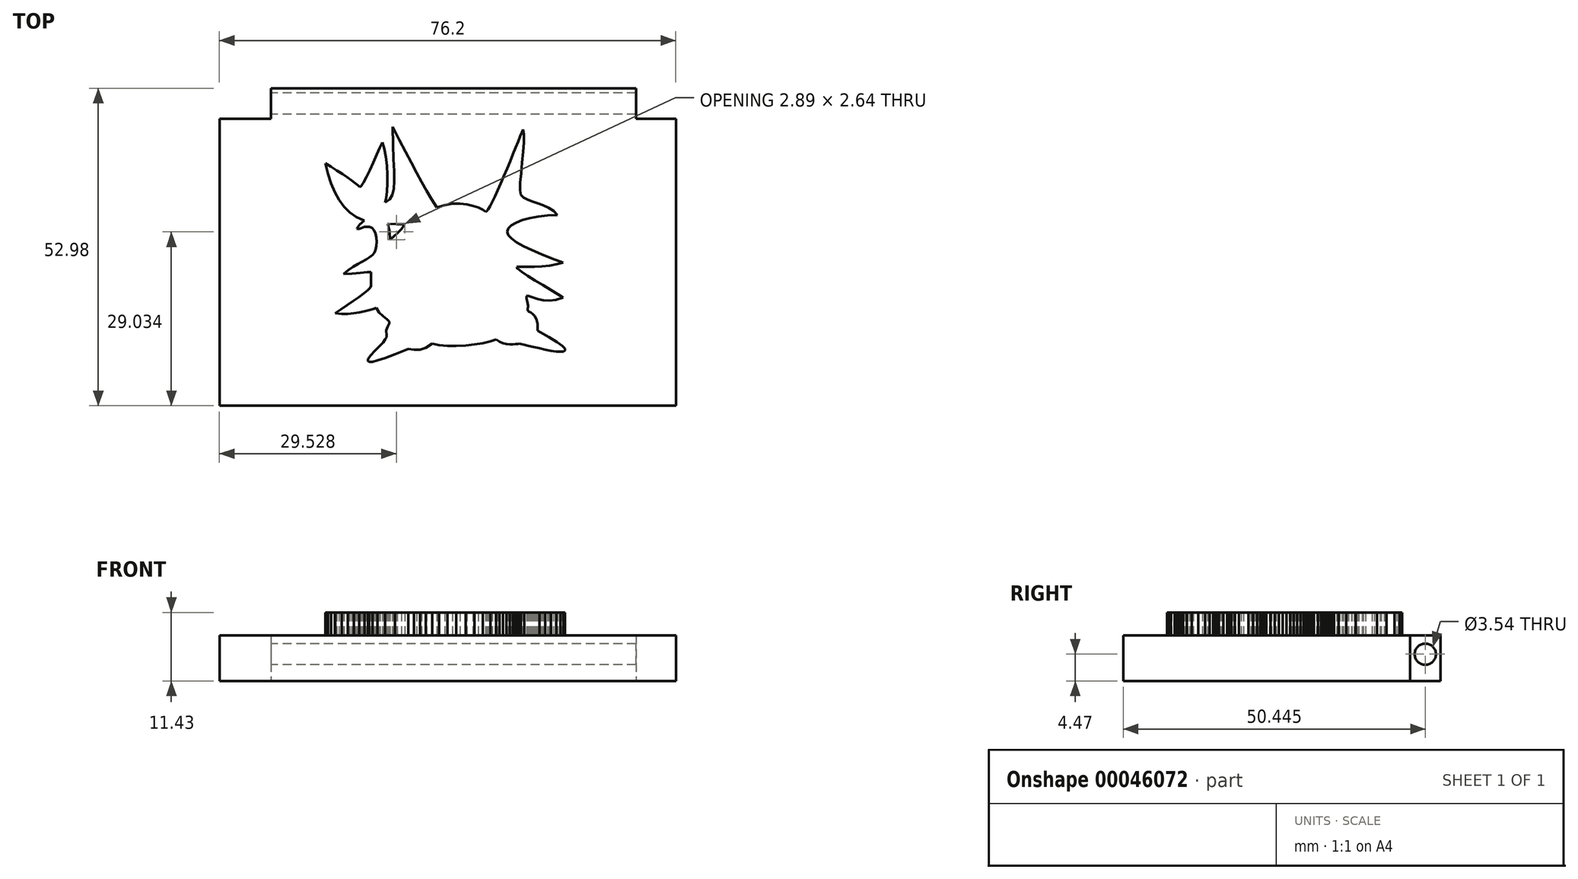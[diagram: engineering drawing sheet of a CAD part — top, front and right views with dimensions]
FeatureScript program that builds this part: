
annotation { "Feature Type Name" : "Feature", "Feature Type Description" : "" }
export const myFeature = defineFeature(function(context is Context, id is Id, definition is map)
    precondition{}
    {
        {
            var Q0;
            Q0=qCreatedBy(makeId("Top.planeOp"),FACE);
            var sketch = newSketch(context, id + "F0", { "sketchPlane" : qUnion([Q0])});
            skLineSegment(sketch, "E0.bottom", {"start": v(-26.13, 37.9) * mm, "end": v(34.83, 37.9) * mm});
            skLineSegment(sketch, "E0.top", {"start": v(-26.13, 32.81) * mm, "end": v(34.83, 32.81) * mm});
            skLineSegment(sketch, "E0.left", {"start": v(-26.13, 37.9) * mm, "end": v(-26.13, 32.81) * mm});
            skLineSegment(sketch, "E0.right", {"start": v(34.83, 37.9) * mm, "end": v(34.83, 32.81) * mm});
            skLineSegment(sketch, "E1.bottom", {"start": v(-34.73, 32.81) * mm, "end": v(41.47, 32.81) * mm});
            skLineSegment(sketch, "E1.top", {"start": v(-34.73, -15.09) * mm, "end": v(41.47, -15.09) * mm});
            skLineSegment(sketch, "E1.left", {"start": v(-34.73, 32.81) * mm, "end": v(-34.73, -15.09) * mm});
            skLineSegment(sketch, "E1.right", {"start": v(41.47, 32.81) * mm, "end": v(41.47, -15.09) * mm});
            skSolve(sketch);
        }
        {
            var Q0;
            Q0=makeQuery(id+"F0.imprint","IMPRINT",FACE,{"disambiguationData":[TD([[makeQuery(id+"F0.imprint","IMPRINT",EDGE,{"derivedFrom":sQuery(id+"F0.wireOp",EDGE,"E1.top")}),1.0]])]});
            var Q1;
            Q1=makeQuery(id+"F0.imprint","IMPRINT",FACE,{"disambiguationData":[TD([[makeQuery(id+"F0.imprint","IMPRINT",EDGE,{"derivedFrom":sQuery(id+"F0.wireOp",EDGE,"E0.bottom")}),-1.0]])]});
            extrude(context, id + "F1", {"entities" : qUnion([Q0, Q1]), "depth" : 7.62 * mm});
        }
        {
            var Q0;
            Q0=makeQuery(id+"F1.opExtrude","SWEPT_FACE",FACE,{"disambiguationData":[OSD([sQuery(id+"F0.wireOp",EDGE,"E0.left")])]});
            var sketch = newSketch(context, id + "F2", { "sketchPlane" : qUnion([Q0])});
            skLineSegment(sketch, "E2", {"start": v(-35.35, 7.62) * mm, "end": v(-35.35, 6.25) * mm});
            skLineSegment(sketch, "E3", {"start": v(-35.35, 6.25) * mm, "end": v(-37.9, 6.25) * mm});
            skLineSegment(sketch, "E4", {"start": v(-35.35, 6.25) * mm, "end": v(-35.35, 4.47) * mm});
            skCircle(sketch, "E5", {"center": v(-35.35, 4.47) * mm, "radius": 1.77 * mm});
            skLineSegment(sketch, "E6", {"start": v(-35.35, 4.47) * mm, "end": v(-37.12, 4.47) * mm});
            skSolve(sketch);
        }
        {
            var Q0;
            {var subQ0=sQuery(id+"F2.wireOp",EDGE,"E6");Q0=makeQuery(id+"F2.imprint","IMPRINT",FACE,{"disambiguationData":[TD([[makeQuery(id+"F2.imprint","IMPRINT",EDGE,{"derivedFrom":subQ0}),-1.0]])]});}
            var Q1;
            {var subQ0=sQuery(id+"F2.wireOp",EDGE,"E6");Q1=makeQuery(id+"F2.imprint","IMPRINT",FACE,{"disambiguationData":[TD([[makeQuery(id+"F2.imprint","IMPRINT",EDGE,{"derivedFrom":subQ0}),1.0]])]});}
            extrude(context, id + "F3", {"entities" : qUnion([Q0, Q1]), "operationType" : NewBodyOperationType.REMOVE, "oppositeDirection" : true, "depth" : 127 * mm});
        }
        {
            var Q0;
            Q0=makeQuery(id+"F1.opExtrude","CAP_FACE",FACE,{"disambiguationData":[OSD([sQuery(id+"F0.wireOp",EDGE,"E0.bottom"),sQuery(id+"F0.wireOp",EDGE,"E0.left"),sQuery(id+"F0.wireOp",EDGE,"E0.right"),sQuery(id+"F0.wireOp",EDGE,"E1.bottom"),sQuery(id+"F0.wireOp",EDGE,"E1.top"),sQuery(id+"F0.wireOp",EDGE,"E1.left"),sQuery(id+"F0.wireOp",EDGE,"E1.right")])],"isStart":false});
            var sketch = newSketch(context, id + "F4", { "sketchPlane" : qUnion([Q0])});
            skLineSegment(sketch, "E7", {"start": v(-8.8, 19.62) * mm, "end": v(-7.67, 17.43) * mm});
            skLineSegment(sketch, "E8", {"start": v(-7.67, 17.43) * mm, "end": v(-6.63, 15.44) * mm});
            skLineSegment(sketch, "E9", {"start": v(-6.63, 15.44) * mm, "end": v(-5.68, 13.62) * mm});
            skLineSegment(sketch, "E10", {"start": v(-5.68, 13.62) * mm, "end": v(-4.78, 11.94) * mm});
            skLineSegment(sketch, "E11", {"start": v(-4.78, 11.94) * mm, "end": v(-3.93, 10.39) * mm});
            skLineSegment(sketch, "E12", {"start": v(-3.93, 10.39) * mm, "end": v(-3.1, 8.93) * mm});
            skLineSegment(sketch, "E13", {"start": v(-3.1, 8.93) * mm, "end": v(-2.27, 7.52) * mm});
            skLineSegment(sketch, "E14", {"start": v(-2.27, 7.52) * mm, "end": v(-1.42, 6.16) * mm});
            skLineSegment(sketch, "E15", {"start": v(-1.42, 6.16) * mm, "end": v(-0.09, 6.56) * mm});
            skLineSegment(sketch, "E16", {"start": v(-0.09, 6.56) * mm, "end": v(1.21, 6.76) * mm});
            skLineSegment(sketch, "E17", {"start": v(1.21, 6.76) * mm, "end": v(2.46, 6.78) * mm});
            skLineSegment(sketch, "E18", {"start": v(2.46, 6.78) * mm, "end": v(3.62, 6.66) * mm});
            skLineSegment(sketch, "E19", {"start": v(3.62, 6.66) * mm, "end": v(4.66, 6.43) * mm});
            skLineSegment(sketch, "E20", {"start": v(4.66, 6.43) * mm, "end": v(5.55, 6.13) * mm});
            skLineSegment(sketch, "E21", {"start": v(5.55, 6.13) * mm, "end": v(6.25, 5.8) * mm});
            skLineSegment(sketch, "E22", {"start": v(6.25, 5.8) * mm, "end": v(6.75, 5.46) * mm});
            skLineSegment(sketch, "E23", {"start": v(6.75, 5.46) * mm, "end": v(6.91, 5.5) * mm});
            skLineSegment(sketch, "E24", {"start": v(6.91, 5.5) * mm, "end": v(7.17, 5.81) * mm});
            skLineSegment(sketch, "E25", {"start": v(7.17, 5.81) * mm, "end": v(7.49, 6.35) * mm});
            skLineSegment(sketch, "E26", {"start": v(7.49, 6.35) * mm, "end": v(7.87, 7.1) * mm});
            skLineSegment(sketch, "E27", {"start": v(7.87, 7.1) * mm, "end": v(8.3, 8) * mm});
            skLineSegment(sketch, "E28", {"start": v(8.3, 8) * mm, "end": v(8.78, 9.04) * mm});
            skLineSegment(sketch, "E29", {"start": v(8.78, 9.04) * mm, "end": v(9.28, 10.17) * mm});
            skLineSegment(sketch, "E30", {"start": v(9.28, 10.17) * mm, "end": v(9.8, 11.37) * mm});
            skLineSegment(sketch, "E31", {"start": v(9.8, 11.37) * mm, "end": v(10.3, 12.6) * mm});
            skLineSegment(sketch, "E32", {"start": v(10.3, 12.6) * mm, "end": v(10.82, 13.83) * mm});
            skLineSegment(sketch, "E33", {"start": v(10.82, 13.83) * mm, "end": v(11.3, 15.01) * mm});
            skLineSegment(sketch, "E34", {"start": v(11.3, 15.01) * mm, "end": v(11.75, 16.13) * mm});
            skLineSegment(sketch, "E35", {"start": v(11.75, 16.13) * mm, "end": v(12.16, 17.14) * mm});
            skLineSegment(sketch, "E36", {"start": v(12.16, 17.14) * mm, "end": v(12.51, 18) * mm});
            skLineSegment(sketch, "E37", {"start": v(12.51, 18) * mm, "end": v(12.8, 18.7) * mm});
            skLineSegment(sketch, "E38", {"start": v(12.8, 18.7) * mm, "end": v(13, 19.2) * mm});
            skLineSegment(sketch, "E39", {"start": v(13, 19.2) * mm, "end": v(13.16, 18.35) * mm});
            skLineSegment(sketch, "E40", {"start": v(13.16, 18.35) * mm, "end": v(13.15, 17.03) * mm});
            skLineSegment(sketch, "E41", {"start": v(13.15, 17.03) * mm, "end": v(13.02, 15.41) * mm});
            skLineSegment(sketch, "E42", {"start": v(13.02, 15.41) * mm, "end": v(12.84, 13.64) * mm});
            skLineSegment(sketch, "E43", {"start": v(12.84, 13.64) * mm, "end": v(12.66, 11.88) * mm});
            skLineSegment(sketch, "E44", {"start": v(12.66, 11.88) * mm, "end": v(12.53, 10.3) * mm});
            skLineSegment(sketch, "E45", {"start": v(12.53, 10.3) * mm, "end": v(12.51, 9.02) * mm});
            skLineSegment(sketch, "E46", {"start": v(12.51, 9.02) * mm, "end": v(12.66, 8.24) * mm});
            skLineSegment(sketch, "E47", {"start": v(12.66, 8.24) * mm, "end": v(13.04, 7.81) * mm});
            skLineSegment(sketch, "E48", {"start": v(13.04, 7.81) * mm, "end": v(13.68, 7.46) * mm});
            skLineSegment(sketch, "E49", {"start": v(13.68, 7.46) * mm, "end": v(14.48, 7.15) * mm});
            skLineSegment(sketch, "E50", {"start": v(14.48, 7.15) * mm, "end": v(15.39, 6.85) * mm});
            skLineSegment(sketch, "E51", {"start": v(15.39, 6.85) * mm, "end": v(16.33, 6.5) * mm});
            skLineSegment(sketch, "E52", {"start": v(16.33, 6.5) * mm, "end": v(17.25, 6.1) * mm});
            skLineSegment(sketch, "E53", {"start": v(17.25, 6.1) * mm, "end": v(18.06, 5.56) * mm});
            skLineSegment(sketch, "E54", {"start": v(18.06, 5.56) * mm, "end": v(18.7, 4.88) * mm});
            skLineSegment(sketch, "E55", {"start": v(18.7, 4.88) * mm, "end": v(17.1, 4.8) * mm});
            skLineSegment(sketch, "E56", {"start": v(17.1, 4.8) * mm, "end": v(15.56, 4.63) * mm});
            skLineSegment(sketch, "E57", {"start": v(15.56, 4.63) * mm, "end": v(14.15, 4.37) * mm});
            skLineSegment(sketch, "E58", {"start": v(14.15, 4.37) * mm, "end": v(12.89, 4.03) * mm});
            skLineSegment(sketch, "E59", {"start": v(12.89, 4.03) * mm, "end": v(11.83, 3.62) * mm});
            skLineSegment(sketch, "E60", {"start": v(11.83, 3.62) * mm, "end": v(11.03, 3.16) * mm});
            skLineSegment(sketch, "E61", {"start": v(11.03, 3.16) * mm, "end": v(10.51, 2.65) * mm});
            skLineSegment(sketch, "E62", {"start": v(10.51, 2.65) * mm, "end": v(10.33, 2.1) * mm});
            skLineSegment(sketch, "E63", {"start": v(10.33, 2.1) * mm, "end": v(10.53, 1.54) * mm});
            skLineSegment(sketch, "E64", {"start": v(10.53, 1.54) * mm, "end": v(11.08, 0.95) * mm});
            skLineSegment(sketch, "E65", {"start": v(11.08, 0.95) * mm, "end": v(11.94, 0.33) * mm});
            skLineSegment(sketch, "E66", {"start": v(11.94, 0.33) * mm, "end": v(13.09, -0.3) * mm});
            skLineSegment(sketch, "E67", {"start": v(13.09, -0.3) * mm, "end": v(14.47, -0.96) * mm});
            skLineSegment(sketch, "E68", {"start": v(14.47, -0.96) * mm, "end": v(16.06, -1.64) * mm});
            skLineSegment(sketch, "E69", {"start": v(16.06, -1.64) * mm, "end": v(17.8, -2.33) * mm});
            skLineSegment(sketch, "E70", {"start": v(17.8, -2.33) * mm, "end": v(19.67, -3.04) * mm});
            skLineSegment(sketch, "E71", {"start": v(19.67, -3.04) * mm, "end": v(18.63, -3.33) * mm});
            skLineSegment(sketch, "E72", {"start": v(18.63, -3.33) * mm, "end": v(17.42, -3.53) * mm});
            skLineSegment(sketch, "E73", {"start": v(17.42, -3.53) * mm, "end": v(16.14, -3.66) * mm});
            skLineSegment(sketch, "E74", {"start": v(16.14, -3.66) * mm, "end": v(14.89, -3.73) * mm});
            skLineSegment(sketch, "E75", {"start": v(14.89, -3.73) * mm, "end": v(13.75, -3.76) * mm});
            skLineSegment(sketch, "E76", {"start": v(13.75, -3.76) * mm, "end": v(12.82, -3.76) * mm});
            skLineSegment(sketch, "E77", {"start": v(12.82, -3.76) * mm, "end": v(12.19, -3.75) * mm});
            skLineSegment(sketch, "E78", {"start": v(12.19, -3.75) * mm, "end": v(11.96, -3.75) * mm});
            skLineSegment(sketch, "E79", {"start": v(11.96, -3.75) * mm, "end": v(12.1, -4.06) * mm});
            skLineSegment(sketch, "E80", {"start": v(12.1, -4.06) * mm, "end": v(12.75, -4.58) * mm});
            skLineSegment(sketch, "E81", {"start": v(12.75, -4.58) * mm, "end": v(13.75, -5.25) * mm});
            skLineSegment(sketch, "E82", {"start": v(13.75, -5.25) * mm, "end": v(15, -6.01) * mm});
            skLineSegment(sketch, "E83", {"start": v(15, -6.01) * mm, "end": v(16.34, -6.82) * mm});
            skLineSegment(sketch, "E84", {"start": v(16.34, -6.82) * mm, "end": v(17.65, -7.61) * mm});
            skLineSegment(sketch, "E85", {"start": v(17.65, -7.61) * mm, "end": v(18.8, -8.33) * mm});
            skLineSegment(sketch, "E86", {"start": v(18.8, -8.33) * mm, "end": v(19.68, -8.92) * mm});
            skLineSegment(sketch, "E87", {"start": v(19.68, -8.92) * mm, "end": v(18.49, -9.3) * mm});
            skLineSegment(sketch, "E88", {"start": v(18.49, -9.3) * mm, "end": v(17.37, -9.42) * mm});
            skLineSegment(sketch, "E89", {"start": v(17.37, -9.42) * mm, "end": v(16.35, -9.34) * mm});
            skLineSegment(sketch, "E90", {"start": v(16.35, -9.34) * mm, "end": v(15.46, -9.14) * mm});
            skLineSegment(sketch, "E91", {"start": v(15.46, -9.14) * mm, "end": v(14.71, -8.9) * mm});
            skLineSegment(sketch, "E92", {"start": v(14.71, -8.9) * mm, "end": v(14.14, -8.69) * mm});
            skLineSegment(sketch, "E93", {"start": v(14.14, -8.69) * mm, "end": v(13.76, -8.58) * mm});
            skLineSegment(sketch, "E94", {"start": v(13.76, -8.58) * mm, "end": v(13.6, -8.66) * mm});
            skLineSegment(sketch, "E95", {"start": v(13.6, -8.66) * mm, "end": v(13.6, -9.1) * mm});
            skLineSegment(sketch, "E96", {"start": v(13.6, -9.1) * mm, "end": v(13.7, -9.6) * mm});
            skLineSegment(sketch, "E97", {"start": v(13.7, -9.6) * mm, "end": v(13.8, -10.22) * mm});
            skLineSegment(sketch, "E98", {"start": v(13.8, -10.22) * mm, "end": v(13.78, -10.96) * mm});
            skLineSegment(sketch, "E99", {"start": v(13.78, -10.96) * mm, "end": v(13.8, -11.13) * mm});
            skLineSegment(sketch, "E100", {"start": v(13.8, -11.13) * mm, "end": v(13.99, -11.26) * mm});
            skLineSegment(sketch, "E101", {"start": v(13.99, -11.26) * mm, "end": v(14.27, -11.4) * mm});
            skLineSegment(sketch, "E102", {"start": v(14.27, -11.4) * mm, "end": v(14.6, -11.6) * mm});
            skLineSegment(sketch, "E103", {"start": v(14.6, -11.6) * mm, "end": v(14.94, -11.95) * mm});
            skLineSegment(sketch, "E104", {"start": v(14.94, -11.95) * mm, "end": v(15.23, -12.5) * mm});
            skLineSegment(sketch, "E105", {"start": v(15.23, -12.5) * mm, "end": v(15.4, -13.3) * mm});
            skLineSegment(sketch, "E106", {"start": v(15.4, -13.3) * mm, "end": v(15.44, -14.43) * mm});
            skLineSegment(sketch, "E107", {"start": v(15.44, -14.43) * mm, "end": v(17.33, -15.5) * mm});
            skLineSegment(sketch, "E108", {"start": v(17.33, -15.5) * mm, "end": v(18.68, -16.34) * mm});
            skLineSegment(sketch, "E109", {"start": v(18.68, -16.34) * mm, "end": v(19.54, -16.98) * mm});
            skLineSegment(sketch, "E110", {"start": v(19.54, -16.98) * mm, "end": v(19.97, -17.43) * mm});
            skLineSegment(sketch, "E111", {"start": v(19.97, -17.43) * mm, "end": v(20.02, -17.73) * mm});
            skLineSegment(sketch, "E112", {"start": v(20.02, -17.73) * mm, "end": v(19.76, -17.9) * mm});
            skLineSegment(sketch, "E113", {"start": v(19.76, -17.9) * mm, "end": v(19.24, -17.94) * mm});
            skLineSegment(sketch, "E114", {"start": v(19.24, -17.94) * mm, "end": v(18.52, -17.88) * mm});
            skLineSegment(sketch, "E115", {"start": v(18.52, -17.88) * mm, "end": v(17.65, -17.76) * mm});
            skLineSegment(sketch, "E116", {"start": v(17.65, -17.76) * mm, "end": v(16.7, -17.58) * mm});
            skLineSegment(sketch, "E117", {"start": v(16.7, -17.58) * mm, "end": v(15.72, -17.37) * mm});
            skLineSegment(sketch, "E118", {"start": v(15.72, -17.37) * mm, "end": v(14.77, -17.15) * mm});
            skLineSegment(sketch, "E119", {"start": v(14.77, -17.15) * mm, "end": v(13.9, -16.94) * mm});
            skLineSegment(sketch, "E120", {"start": v(13.9, -16.94) * mm, "end": v(13.18, -16.77) * mm});
            skLineSegment(sketch, "E121", {"start": v(13.18, -16.77) * mm, "end": v(12.66, -16.65) * mm});
            skLineSegment(sketch, "E122", {"start": v(12.66, -16.65) * mm, "end": v(12.4, -16.6) * mm});
            skLineSegment(sketch, "E123", {"start": v(12.4, -16.6) * mm, "end": v(12.11, -16.63) * mm});
            skLineSegment(sketch, "E124", {"start": v(12.11, -16.63) * mm, "end": v(11.73, -16.67) * mm});
            skLineSegment(sketch, "E125", {"start": v(11.73, -16.67) * mm, "end": v(11.28, -16.7) * mm});
            skLineSegment(sketch, "E126", {"start": v(11.28, -16.7) * mm, "end": v(10.77, -16.7) * mm});
            skLineSegment(sketch, "E127", {"start": v(10.77, -16.7) * mm, "end": v(10.21, -16.66) * mm});
            skLineSegment(sketch, "E128", {"start": v(10.21, -16.66) * mm, "end": v(9.63, -16.53) * mm});
            skLineSegment(sketch, "E129", {"start": v(9.63, -16.53) * mm, "end": v(9.05, -16.28) * mm});
            skLineSegment(sketch, "E130", {"start": v(9.05, -16.28) * mm, "end": v(8.48, -15.91) * mm});
            skLineSegment(sketch, "E131", {"start": v(8.48, -15.91) * mm, "end": v(7.52, -16.21) * mm});
            skLineSegment(sketch, "E132", {"start": v(7.52, -16.21) * mm, "end": v(6.3, -16.49) * mm});
            skLineSegment(sketch, "E133", {"start": v(6.3, -16.49) * mm, "end": v(4.9, -16.72) * mm});
            skLineSegment(sketch, "E134", {"start": v(4.9, -16.72) * mm, "end": v(3.39, -16.89) * mm});
            skLineSegment(sketch, "E135", {"start": v(3.39, -16.89) * mm, "end": v(1.85, -16.97) * mm});
            skLineSegment(sketch, "E136", {"start": v(1.85, -16.97) * mm, "end": v(0.35, -16.97) * mm});
            skLineSegment(sketch, "E137", {"start": v(0.35, -16.97) * mm, "end": v(-1.02, -16.85) * mm});
            skLineSegment(sketch, "E138", {"start": v(-1.02, -16.85) * mm, "end": v(-2.2, -16.6) * mm});
            skLineSegment(sketch, "E139", {"start": v(-2.2, -16.6) * mm, "end": v(-3.22, -17.28) * mm});
            skLineSegment(sketch, "E140", {"start": v(-3.22, -17.28) * mm, "end": v(-4.21, -17.58) * mm});
            skLineSegment(sketch, "E141", {"start": v(-4.21, -17.58) * mm, "end": v(-5.2, -17.61) * mm});
            skLineSegment(sketch, "E142", {"start": v(-5.2, -17.61) * mm, "end": v(-6.2, -17.48) * mm});
            skLineSegment(sketch, "E143", {"start": v(-6.2, -17.48) * mm, "end": v(-8.37, -18.36) * mm});
            skLineSegment(sketch, "E144", {"start": v(-8.37, -18.36) * mm, "end": v(-10.06, -19) * mm});
            skLineSegment(sketch, "E145", {"start": v(-10.06, -19) * mm, "end": v(-11.3, -19.4) * mm});
            skLineSegment(sketch, "E146", {"start": v(-11.3, -19.4) * mm, "end": v(-12.16, -19.6) * mm});
            skLineSegment(sketch, "E147", {"start": v(-12.16, -19.6) * mm, "end": v(-12.68, -19.62) * mm});
            skLineSegment(sketch, "E148", {"start": v(-12.68, -19.62) * mm, "end": v(-12.91, -19.5) * mm});
            skLineSegment(sketch, "E149", {"start": v(-12.91, -19.5) * mm, "end": v(-12.9, -19.24) * mm});
            skLineSegment(sketch, "E150", {"start": v(-12.9, -19.24) * mm, "end": v(-12.68, -18.87) * mm});
            skLineSegment(sketch, "E151", {"start": v(-12.68, -18.87) * mm, "end": v(-12.32, -18.43) * mm});
            skLineSegment(sketch, "E152", {"start": v(-12.32, -18.43) * mm, "end": v(-11.87, -17.94) * mm});
            skLineSegment(sketch, "E153", {"start": v(-11.87, -17.94) * mm, "end": v(-11.36, -17.41) * mm});
            skLineSegment(sketch, "E154", {"start": v(-11.36, -17.41) * mm, "end": v(-10.85, -16.88) * mm});
            skLineSegment(sketch, "E155", {"start": v(-10.85, -16.88) * mm, "end": v(-10.39, -16.37) * mm});
            skLineSegment(sketch, "E156", {"start": v(-10.39, -16.37) * mm, "end": v(-10.02, -15.9) * mm});
            skLineSegment(sketch, "E157", {"start": v(-10.02, -15.9) * mm, "end": v(-9.8, -15.52) * mm});
            skLineSegment(sketch, "E158", {"start": v(-9.8, -15.52) * mm, "end": v(-9.76, -15.22) * mm});
            skLineSegment(sketch, "E159", {"start": v(-9.76, -15.22) * mm, "end": v(-9.84, -14.36) * mm});
            skLineSegment(sketch, "E160", {"start": v(-9.84, -14.36) * mm, "end": v(-9.62, -13.72) * mm});
            skLineSegment(sketch, "E161", {"start": v(-9.62, -13.72) * mm, "end": v(-9.36, -13.24) * mm});
            skLineSegment(sketch, "E162", {"start": v(-9.36, -13.24) * mm, "end": v(-9.33, -12.87) * mm});
            skLineSegment(sketch, "E163", {"start": v(-9.33, -12.87) * mm, "end": v(-9.71, -12.49) * mm});
            skLineSegment(sketch, "E164", {"start": v(-9.71, -12.49) * mm, "end": v(-10.38, -12) * mm});
            skLineSegment(sketch, "E165", {"start": v(-10.38, -12) * mm, "end": v(-11.06, -11.38) * mm});
            skLineSegment(sketch, "E166", {"start": v(-11.06, -11.38) * mm, "end": v(-11.5, -10.61) * mm});
            skLineSegment(sketch, "E167", {"start": v(-11.5, -10.61) * mm, "end": v(-12.03, -10.79) * mm});
            skLineSegment(sketch, "E168", {"start": v(-12.03, -10.79) * mm, "end": v(-12.7, -10.99) * mm});
            skLineSegment(sketch, "E169", {"start": v(-12.7, -10.99) * mm, "end": v(-13.47, -11.19) * mm});
            skLineSegment(sketch, "E170", {"start": v(-13.47, -11.19) * mm, "end": v(-14.34, -11.37) * mm});
            skLineSegment(sketch, "E171", {"start": v(-14.34, -11.37) * mm, "end": v(-15.28, -11.52) * mm});
            skLineSegment(sketch, "E172", {"start": v(-15.28, -11.52) * mm, "end": v(-16.27, -11.6) * mm});
            skLineSegment(sketch, "E173", {"start": v(-16.27, -11.6) * mm, "end": v(-17.3, -11.6) * mm});
            skLineSegment(sketch, "E174", {"start": v(-17.3, -11.6) * mm, "end": v(-18.36, -11.5) * mm});
            skLineSegment(sketch, "E175", {"start": v(-18.36, -11.5) * mm, "end": v(-17.4, -10.85) * mm});
            skLineSegment(sketch, "E176", {"start": v(-17.4, -10.85) * mm, "end": v(-16.38, -10.18) * mm});
            skLineSegment(sketch, "E177", {"start": v(-16.38, -10.18) * mm, "end": v(-15.37, -9.5) * mm});
            skLineSegment(sketch, "E178", {"start": v(-15.37, -9.5) * mm, "end": v(-14.43, -8.84) * mm});
            skLineSegment(sketch, "E179", {"start": v(-14.43, -8.84) * mm, "end": v(-13.6, -8.23) * mm});
            skLineSegment(sketch, "E180", {"start": v(-13.6, -8.23) * mm, "end": v(-12.95, -7.68) * mm});
            skLineSegment(sketch, "E181", {"start": v(-12.95, -7.68) * mm, "end": v(-12.52, -7.23) * mm});
            skLineSegment(sketch, "E182", {"start": v(-12.52, -7.23) * mm, "end": v(-12.37, -6.9) * mm});
            skLineSegment(sketch, "E183", {"start": v(-12.37, -6.9) * mm, "end": v(-12.38, -6.3) * mm});
            skLineSegment(sketch, "E184", {"start": v(-12.38, -6.3) * mm, "end": v(-12.39, -5.66) * mm});
            skLineSegment(sketch, "E185", {"start": v(-12.39, -5.66) * mm, "end": v(-12.39, -5.06) * mm});
            skLineSegment(sketch, "E186", {"start": v(-12.39, -5.06) * mm, "end": v(-12.37, -4.62) * mm});
            skLineSegment(sketch, "E187", {"start": v(-12.37, -4.62) * mm, "end": v(-13.04, -4.66) * mm});
            skLineSegment(sketch, "E188", {"start": v(-13.04, -4.66) * mm, "end": v(-14.18, -4.77) * mm});
            skLineSegment(sketch, "E189", {"start": v(-14.18, -4.77) * mm, "end": v(-15.57, -4.89) * mm});
            skLineSegment(sketch, "E190", {"start": v(-15.57, -4.89) * mm, "end": v(-16.97, -4.96) * mm});
            skLineSegment(sketch, "E191", {"start": v(-16.97, -4.96) * mm, "end": v(-16.2, -4.32) * mm});
            skLineSegment(sketch, "E192", {"start": v(-16.2, -4.32) * mm, "end": v(-15.4, -3.78) * mm});
            skLineSegment(sketch, "E193", {"start": v(-15.4, -3.78) * mm, "end": v(-14.62, -3.31) * mm});
            skLineSegment(sketch, "E194", {"start": v(-14.62, -3.31) * mm, "end": v(-13.89, -2.9) * mm});
            skLineSegment(sketch, "E195", {"start": v(-13.89, -2.9) * mm, "end": v(-13.22, -2.52) * mm});
            skLineSegment(sketch, "E196", {"start": v(-13.22, -2.52) * mm, "end": v(-12.63, -2.16) * mm});
            skLineSegment(sketch, "E197", {"start": v(-12.63, -2.16) * mm, "end": v(-12.17, -1.8) * mm});
            skLineSegment(sketch, "E198", {"start": v(-12.17, -1.8) * mm, "end": v(-11.85, -1.4) * mm});
            skLineSegment(sketch, "E199", {"start": v(-11.85, -1.4) * mm, "end": v(-11.64, -0.9) * mm});
            skLineSegment(sketch, "E200", {"start": v(-11.64, -0.9) * mm, "end": v(-11.5, -0.29) * mm});
            skLineSegment(sketch, "E201", {"start": v(-11.5, -0.29) * mm, "end": v(-11.46, 0.4) * mm});
            skLineSegment(sketch, "E202", {"start": v(-11.46, 0.4) * mm, "end": v(-11.5, 1.12) * mm});
            skLineSegment(sketch, "E203", {"start": v(-11.5, 1.12) * mm, "end": v(-11.63, 1.78) * mm});
            skLineSegment(sketch, "E204", {"start": v(-11.63, 1.78) * mm, "end": v(-11.86, 2.35) * mm});
            skLineSegment(sketch, "E205", {"start": v(-11.86, 2.35) * mm, "end": v(-12.2, 2.75) * mm});
            skLineSegment(sketch, "E206", {"start": v(-12.2, 2.75) * mm, "end": v(-12.63, 2.94) * mm});
            skLineSegment(sketch, "E207", {"start": v(-12.63, 2.94) * mm, "end": v(-13.48, 2.9) * mm});
            skLineSegment(sketch, "E208", {"start": v(-13.48, 2.9) * mm, "end": v(-14.09, 2.69) * mm});
            skLineSegment(sketch, "E209", {"start": v(-14.09, 2.69) * mm, "end": v(-14.5, 2.52) * mm});
            skLineSegment(sketch, "E210", {"start": v(-14.5, 2.52) * mm, "end": v(-14.76, 2.63) * mm});
            skLineSegment(sketch, "E211", {"start": v(-14.76, 2.63) * mm, "end": v(-14.64, 2.87) * mm});
            skLineSegment(sketch, "E212", {"start": v(-14.64, 2.87) * mm, "end": v(-14.46, 3.11) * mm});
            skLineSegment(sketch, "E213", {"start": v(-14.46, 3.11) * mm, "end": v(-14.22, 3.34) * mm});
            skLineSegment(sketch, "E214", {"start": v(-14.22, 3.34) * mm, "end": v(-13.98, 3.55) * mm});
            skLineSegment(sketch, "E215", {"start": v(-13.98, 3.55) * mm, "end": v(-13.76, 3.73) * mm});
            skLineSegment(sketch, "E216", {"start": v(-13.76, 3.73) * mm, "end": v(-13.6, 3.86) * mm});
            skLineSegment(sketch, "E217", {"start": v(-13.6, 3.86) * mm, "end": v(-13.53, 3.95) * mm});
            skLineSegment(sketch, "E218", {"start": v(-13.53, 3.95) * mm, "end": v(-13.58, 3.99) * mm});
            skLineSegment(sketch, "E219", {"start": v(-13.58, 3.99) * mm, "end": v(-14.87, 4.58) * mm});
            skLineSegment(sketch, "E220", {"start": v(-14.87, 4.58) * mm, "end": v(-15.98, 5.35) * mm});
            skLineSegment(sketch, "E221", {"start": v(-15.98, 5.35) * mm, "end": v(-16.93, 6.29) * mm});
            skLineSegment(sketch, "E222", {"start": v(-16.93, 6.29) * mm, "end": v(-17.74, 7.4) * mm});
            skLineSegment(sketch, "E223", {"start": v(-17.74, 7.4) * mm, "end": v(-18.43, 8.68) * mm});
            skLineSegment(sketch, "E224", {"start": v(-18.43, 8.68) * mm, "end": v(-19.03, 10.13) * mm});
            skLineSegment(sketch, "E225", {"start": v(-19.03, 10.13) * mm, "end": v(-19.55, 11.75) * mm});
            skLineSegment(sketch, "E226", {"start": v(-19.55, 11.75) * mm, "end": v(-20.02, 13.53) * mm});
            skLineSegment(sketch, "E227", {"start": v(-20.02, 13.53) * mm, "end": v(-19.04, 12.93) * mm});
            skLineSegment(sketch, "E228", {"start": v(-19.04, 12.93) * mm, "end": v(-18.09, 12.32) * mm});
            skLineSegment(sketch, "E229", {"start": v(-18.09, 12.32) * mm, "end": v(-17.19, 11.72) * mm});
            skLineSegment(sketch, "E230", {"start": v(-17.19, 11.72) * mm, "end": v(-16.36, 11.16) * mm});
            skLineSegment(sketch, "E231", {"start": v(-16.36, 11.16) * mm, "end": v(-15.64, 10.65) * mm});
            skLineSegment(sketch, "E232", {"start": v(-15.64, 10.65) * mm, "end": v(-15.03, 10.2) * mm});
            skLineSegment(sketch, "E233", {"start": v(-15.03, 10.2) * mm, "end": v(-14.58, 9.85) * mm});
            skLineSegment(sketch, "E234", {"start": v(-14.58, 9.85) * mm, "end": v(-14.3, 9.6) * mm});
            skLineSegment(sketch, "E235", {"start": v(-14.3, 9.6) * mm, "end": v(-14.03, 9.7) * mm});
            skLineSegment(sketch, "E236", {"start": v(-14.03, 9.7) * mm, "end": v(-13.64, 10.27) * mm});
            skLineSegment(sketch, "E237", {"start": v(-13.64, 10.27) * mm, "end": v(-13.15, 11.2) * mm});
            skLineSegment(sketch, "E238", {"start": v(-13.15, 11.2) * mm, "end": v(-12.6, 12.37) * mm});
            skLineSegment(sketch, "E239", {"start": v(-12.6, 12.37) * mm, "end": v(-12.04, 13.66) * mm});
            skLineSegment(sketch, "E240", {"start": v(-12.04, 13.66) * mm, "end": v(-11.47, 14.95) * mm});
            skLineSegment(sketch, "E241", {"start": v(-11.47, 14.95) * mm, "end": v(-10.94, 16.11) * mm});
            skLineSegment(sketch, "E242", {"start": v(-10.94, 16.11) * mm, "end": v(-10.47, 17.04) * mm});
            skLineSegment(sketch, "E243", {"start": v(-10.47, 17.04) * mm, "end": v(-10.14, 15.94) * mm});
            skLineSegment(sketch, "E244", {"start": v(-10.14, 15.94) * mm, "end": v(-9.9, 14.62) * mm});
            skLineSegment(sketch, "E245", {"start": v(-9.9, 14.62) * mm, "end": v(-9.74, 13.15) * mm});
            skLineSegment(sketch, "E246", {"start": v(-9.74, 13.15) * mm, "end": v(-9.66, 11.64) * mm});
            skLineSegment(sketch, "E247", {"start": v(-9.66, 11.64) * mm, "end": v(-9.65, 10.18) * mm});
            skLineSegment(sketch, "E248", {"start": v(-9.65, 10.18) * mm, "end": v(-9.72, 8.85) * mm});
            skLineSegment(sketch, "E249", {"start": v(-9.72, 8.85) * mm, "end": v(-9.85, 7.74) * mm});
            skLineSegment(sketch, "E250", {"start": v(-9.85, 7.74) * mm, "end": v(-10.04, 6.96) * mm});
            skLineSegment(sketch, "E251", {"start": v(-10.04, 6.96) * mm, "end": v(-9.3, 7.5) * mm});
            skLineSegment(sketch, "E252", {"start": v(-9.3, 7.5) * mm, "end": v(-8.83, 8.24) * mm});
            skLineSegment(sketch, "E253", {"start": v(-8.83, 8.24) * mm, "end": v(-8.57, 9.23) * mm});
            skLineSegment(sketch, "E254", {"start": v(-8.57, 9.23) * mm, "end": v(-8.49, 10.52) * mm});
            skLineSegment(sketch, "E255", {"start": v(-8.49, 10.52) * mm, "end": v(-8.52, 12.16) * mm});
            skLineSegment(sketch, "E256", {"start": v(-8.52, 12.16) * mm, "end": v(-8.62, 14.19) * mm});
            skLineSegment(sketch, "E257", {"start": v(-8.62, 14.19) * mm, "end": v(-8.73, 16.66) * mm});
            skLineSegment(sketch, "E258", {"start": v(-8.73, 16.66) * mm, "end": v(-8.8, 19.62) * mm});
            skLineSegment(sketch, "E259", {"start": v(-9.24, 0.76) * mm, "end": v(-8.66, 1.24) * mm});
            skLineSegment(sketch, "E260", {"start": v(-8.66, 1.24) * mm, "end": v(-8, 1.85) * mm});
            skLineSegment(sketch, "E261", {"start": v(-8, 1.85) * mm, "end": v(-7.34, 2.55) * mm});
            skLineSegment(sketch, "E262", {"start": v(-7.34, 2.55) * mm, "end": v(-6.72, 3.34) * mm});
            skLineSegment(sketch, "E263", {"start": v(-6.72, 3.34) * mm, "end": v(-8.23, 3.38) * mm});
            skLineSegment(sketch, "E264", {"start": v(-8.23, 3.38) * mm, "end": v(-9.61, 3.4) * mm});
            skLineSegment(sketch, "E265", {"start": v(-9.61, 3.4) * mm, "end": v(-9.3, 2.18) * mm});
            skLineSegment(sketch, "E266", {"start": v(-9.3, 2.18) * mm, "end": v(-9.24, 0.76) * mm});
            skSolve(sketch);
        }
        {
            var Q0;
            Q0 = qSketchRegion(id + "F4", true);
            var Q1;
            Q1=makeQuery(id+"F4.imprint","IMPRINT",FACE,{"disambiguationData":[TD([[makeQuery(id+"F4.imprint","IMPRINT",EDGE,{"derivedFrom":sQuery(id+"F4.wireOp",EDGE,"E7")}),-1.0]])]});
            extrude(context, id + "F5", {"entities" : qUnion([Q0, Q1]), "depth" : 3.8 * mm});
        }
        {
            var Q0;
            Q0=makeQuery(id+"F5.opExtrude","SWEPT_BODY",BODY,{"disambiguationData":[OSD([sQuery(id+"F4.wireOp",EDGE,"E7"),sQuery(id+"F4.wireOp",EDGE,"E8"),sQuery(id+"F4.wireOp",EDGE,"E9"),sQuery(id+"F4.wireOp",EDGE,"E10"),sQuery(id+"F4.wireOp",EDGE,"E11"),sQuery(id+"F4.wireOp",EDGE,"E12"),sQuery(id+"F4.wireOp",EDGE,"E13"),sQuery(id+"F4.wireOp",EDGE,"E14"),sQuery(id+"F4.wireOp",EDGE,"E15"),sQuery(id+"F4.wireOp",EDGE,"E16"),sQuery(id+"F4.wireOp",EDGE,"E17"),sQuery(id+"F4.wireOp",EDGE,"E18"),sQuery(id+"F4.wireOp",EDGE,"E19"),sQuery(id+"F4.wireOp",EDGE,"E20"),sQuery(id+"F4.wireOp",EDGE,"E21"),sQuery(id+"F4.wireOp",EDGE,"E22"),sQuery(id+"F4.wireOp",EDGE,"E23"),sQuery(id+"F4.wireOp",EDGE,"E24"),sQuery(id+"F4.wireOp",EDGE,"E25"),sQuery(id+"F4.wireOp",EDGE,"E26"),sQuery(id+"F4.wireOp",EDGE,"E27"),sQuery(id+"F4.wireOp",EDGE,"E28"),sQuery(id+"F4.wireOp",EDGE,"E29"),sQuery(id+"F4.wireOp",EDGE,"E30"),sQuery(id+"F4.wireOp",EDGE,"E31"),sQuery(id+"F4.wireOp",EDGE,"E32"),sQuery(id+"F4.wireOp",EDGE,"E33"),sQuery(id+"F4.wireOp",EDGE,"E34"),sQuery(id+"F4.wireOp",EDGE,"E35"),sQuery(id+"F4.wireOp",EDGE,"E36"),sQuery(id+"F4.wireOp",EDGE,"E37"),sQuery(id+"F4.wireOp",EDGE,"E38"),sQuery(id+"F4.wireOp",EDGE,"E39"),sQuery(id+"F4.wireOp",EDGE,"E40"),sQuery(id+"F4.wireOp",EDGE,"E41"),sQuery(id+"F4.wireOp",EDGE,"E42"),sQuery(id+"F4.wireOp",EDGE,"E43"),sQuery(id+"F4.wireOp",EDGE,"E44"),sQuery(id+"F4.wireOp",EDGE,"E45"),sQuery(id+"F4.wireOp",EDGE,"E46"),sQuery(id+"F4.wireOp",EDGE,"E47"),sQuery(id+"F4.wireOp",EDGE,"E48"),sQuery(id+"F4.wireOp",EDGE,"E49"),sQuery(id+"F4.wireOp",EDGE,"E50"),sQuery(id+"F4.wireOp",EDGE,"E51"),sQuery(id+"F4.wireOp",EDGE,"E52"),sQuery(id+"F4.wireOp",EDGE,"E53"),sQuery(id+"F4.wireOp",EDGE,"E54"),sQuery(id+"F4.wireOp",EDGE,"E55"),sQuery(id+"F4.wireOp",EDGE,"E56"),sQuery(id+"F4.wireOp",EDGE,"E57"),sQuery(id+"F4.wireOp",EDGE,"E58"),sQuery(id+"F4.wireOp",EDGE,"E59"),sQuery(id+"F4.wireOp",EDGE,"E60"),sQuery(id+"F4.wireOp",EDGE,"E61"),sQuery(id+"F4.wireOp",EDGE,"E62"),sQuery(id+"F4.wireOp",EDGE,"E63"),sQuery(id+"F4.wireOp",EDGE,"E64"),sQuery(id+"F4.wireOp",EDGE,"E65"),sQuery(id+"F4.wireOp",EDGE,"E66"),sQuery(id+"F4.wireOp",EDGE,"E67"),sQuery(id+"F4.wireOp",EDGE,"E68"),sQuery(id+"F4.wireOp",EDGE,"E69"),sQuery(id+"F4.wireOp",EDGE,"E70"),sQuery(id+"F4.wireOp",EDGE,"E71"),sQuery(id+"F4.wireOp",EDGE,"E72"),sQuery(id+"F4.wireOp",EDGE,"E73"),sQuery(id+"F4.wireOp",EDGE,"E74"),sQuery(id+"F4.wireOp",EDGE,"E75"),sQuery(id+"F4.wireOp",EDGE,"E76"),sQuery(id+"F4.wireOp",EDGE,"E77"),sQuery(id+"F4.wireOp",EDGE,"E78"),sQuery(id+"F4.wireOp",EDGE,"E79"),sQuery(id+"F4.wireOp",EDGE,"E80"),sQuery(id+"F4.wireOp",EDGE,"E81"),sQuery(id+"F4.wireOp",EDGE,"E82"),sQuery(id+"F4.wireOp",EDGE,"E83"),sQuery(id+"F4.wireOp",EDGE,"E84"),sQuery(id+"F4.wireOp",EDGE,"E85"),sQuery(id+"F4.wireOp",EDGE,"E86"),sQuery(id+"F4.wireOp",EDGE,"E87"),sQuery(id+"F4.wireOp",EDGE,"E88"),sQuery(id+"F4.wireOp",EDGE,"E89"),sQuery(id+"F4.wireOp",EDGE,"E90"),sQuery(id+"F4.wireOp",EDGE,"E91"),sQuery(id+"F4.wireOp",EDGE,"E92"),sQuery(id+"F4.wireOp",EDGE,"E93"),sQuery(id+"F4.wireOp",EDGE,"E94"),sQuery(id+"F4.wireOp",EDGE,"E95"),sQuery(id+"F4.wireOp",EDGE,"E96"),sQuery(id+"F4.wireOp",EDGE,"E97"),sQuery(id+"F4.wireOp",EDGE,"E98"),sQuery(id+"F4.wireOp",EDGE,"E99"),sQuery(id+"F4.wireOp",EDGE,"E100"),sQuery(id+"F4.wireOp",EDGE,"E101"),sQuery(id+"F4.wireOp",EDGE,"E102"),sQuery(id+"F4.wireOp",EDGE,"E103"),sQuery(id+"F4.wireOp",EDGE,"E104"),sQuery(id+"F4.wireOp",EDGE,"E105"),sQuery(id+"F4.wireOp",EDGE,"E106"),sQuery(id+"F4.wireOp",EDGE,"E107"),sQuery(id+"F4.wireOp",EDGE,"E108"),sQuery(id+"F4.wireOp",EDGE,"E109"),sQuery(id+"F4.wireOp",EDGE,"E110"),sQuery(id+"F4.wireOp",EDGE,"E111"),sQuery(id+"F4.wireOp",EDGE,"E112"),sQuery(id+"F4.wireOp",EDGE,"E113"),sQuery(id+"F4.wireOp",EDGE,"E114"),sQuery(id+"F4.wireOp",EDGE,"E115"),sQuery(id+"F4.wireOp",EDGE,"E116"),sQuery(id+"F4.wireOp",EDGE,"E117"),sQuery(id+"F4.wireOp",EDGE,"E118"),sQuery(id+"F4.wireOp",EDGE,"E119"),sQuery(id+"F4.wireOp",EDGE,"E120"),sQuery(id+"F4.wireOp",EDGE,"E121"),sQuery(id+"F4.wireOp",EDGE,"E122"),sQuery(id+"F4.wireOp",EDGE,"E123"),sQuery(id+"F4.wireOp",EDGE,"E124"),sQuery(id+"F4.wireOp",EDGE,"E125"),sQuery(id+"F4.wireOp",EDGE,"E126"),sQuery(id+"F4.wireOp",EDGE,"E127"),sQuery(id+"F4.wireOp",EDGE,"E128"),sQuery(id+"F4.wireOp",EDGE,"E129"),sQuery(id+"F4.wireOp",EDGE,"E130"),sQuery(id+"F4.wireOp",EDGE,"E131"),sQuery(id+"F4.wireOp",EDGE,"E132"),sQuery(id+"F4.wireOp",EDGE,"E133"),sQuery(id+"F4.wireOp",EDGE,"E134"),sQuery(id+"F4.wireOp",EDGE,"E135"),sQuery(id+"F4.wireOp",EDGE,"E136"),sQuery(id+"F4.wireOp",EDGE,"E137"),sQuery(id+"F4.wireOp",EDGE,"E138"),sQuery(id+"F4.wireOp",EDGE,"E139"),sQuery(id+"F4.wireOp",EDGE,"E140"),sQuery(id+"F4.wireOp",EDGE,"E141"),sQuery(id+"F4.wireOp",EDGE,"E142"),sQuery(id+"F4.wireOp",EDGE,"E143"),sQuery(id+"F4.wireOp",EDGE,"E144"),sQuery(id+"F4.wireOp",EDGE,"E145"),sQuery(id+"F4.wireOp",EDGE,"E146"),sQuery(id+"F4.wireOp",EDGE,"E147"),sQuery(id+"F4.wireOp",EDGE,"E148"),sQuery(id+"F4.wireOp",EDGE,"E149"),sQuery(id+"F4.wireOp",EDGE,"E150"),sQuery(id+"F4.wireOp",EDGE,"E151"),sQuery(id+"F4.wireOp",EDGE,"E152"),sQuery(id+"F4.wireOp",EDGE,"E153"),sQuery(id+"F4.wireOp",EDGE,"E154"),sQuery(id+"F4.wireOp",EDGE,"E155"),sQuery(id+"F4.wireOp",EDGE,"E156"),sQuery(id+"F4.wireOp",EDGE,"E157"),sQuery(id+"F4.wireOp",EDGE,"E158"),sQuery(id+"F4.wireOp",EDGE,"E159"),sQuery(id+"F4.wireOp",EDGE,"E160"),sQuery(id+"F4.wireOp",EDGE,"E161"),sQuery(id+"F4.wireOp",EDGE,"E162"),sQuery(id+"F4.wireOp",EDGE,"E163"),sQuery(id+"F4.wireOp",EDGE,"E164"),sQuery(id+"F4.wireOp",EDGE,"E165"),sQuery(id+"F4.wireOp",EDGE,"E166"),sQuery(id+"F4.wireOp",EDGE,"E167"),sQuery(id+"F4.wireOp",EDGE,"E168"),sQuery(id+"F4.wireOp",EDGE,"E169"),sQuery(id+"F4.wireOp",EDGE,"E170"),sQuery(id+"F4.wireOp",EDGE,"E171"),sQuery(id+"F4.wireOp",EDGE,"E172"),sQuery(id+"F4.wireOp",EDGE,"E173"),sQuery(id+"F4.wireOp",EDGE,"E174"),sQuery(id+"F4.wireOp",EDGE,"E175"),sQuery(id+"F4.wireOp",EDGE,"E176"),sQuery(id+"F4.wireOp",EDGE,"E177"),sQuery(id+"F4.wireOp",EDGE,"E178"),sQuery(id+"F4.wireOp",EDGE,"E179"),sQuery(id+"F4.wireOp",EDGE,"E180"),sQuery(id+"F4.wireOp",EDGE,"E181"),sQuery(id+"F4.wireOp",EDGE,"E182"),sQuery(id+"F4.wireOp",EDGE,"E183"),sQuery(id+"F4.wireOp",EDGE,"E184"),sQuery(id+"F4.wireOp",EDGE,"E185"),sQuery(id+"F4.wireOp",EDGE,"E186"),sQuery(id+"F4.wireOp",EDGE,"E187"),sQuery(id+"F4.wireOp",EDGE,"E188"),sQuery(id+"F4.wireOp",EDGE,"E189"),sQuery(id+"F4.wireOp",EDGE,"E190"),sQuery(id+"F4.wireOp",EDGE,"E191"),sQuery(id+"F4.wireOp",EDGE,"E192"),sQuery(id+"F4.wireOp",EDGE,"E193"),sQuery(id+"F4.wireOp",EDGE,"E194"),sQuery(id+"F4.wireOp",EDGE,"E195"),sQuery(id+"F4.wireOp",EDGE,"E196"),sQuery(id+"F4.wireOp",EDGE,"E197"),sQuery(id+"F4.wireOp",EDGE,"E198"),sQuery(id+"F4.wireOp",EDGE,"E199"),sQuery(id+"F4.wireOp",EDGE,"E200"),sQuery(id+"F4.wireOp",EDGE,"E201"),sQuery(id+"F4.wireOp",EDGE,"E202"),sQuery(id+"F4.wireOp",EDGE,"E203"),sQuery(id+"F4.wireOp",EDGE,"E204"),sQuery(id+"F4.wireOp",EDGE,"E205"),sQuery(id+"F4.wireOp",EDGE,"E206"),sQuery(id+"F4.wireOp",EDGE,"E207"),sQuery(id+"F4.wireOp",EDGE,"E208"),sQuery(id+"F4.wireOp",EDGE,"E209"),sQuery(id+"F4.wireOp",EDGE,"E210"),sQuery(id+"F4.wireOp",EDGE,"E211"),sQuery(id+"F4.wireOp",EDGE,"E212"),sQuery(id+"F4.wireOp",EDGE,"E213"),sQuery(id+"F4.wireOp",EDGE,"E214"),sQuery(id+"F4.wireOp",EDGE,"E215"),sQuery(id+"F4.wireOp",EDGE,"E216"),sQuery(id+"F4.wireOp",EDGE,"E217"),sQuery(id+"F4.wireOp",EDGE,"E218"),sQuery(id+"F4.wireOp",EDGE,"E219"),sQuery(id+"F4.wireOp",EDGE,"E220"),sQuery(id+"F4.wireOp",EDGE,"E221"),sQuery(id+"F4.wireOp",EDGE,"E222"),sQuery(id+"F4.wireOp",EDGE,"E223"),sQuery(id+"F4.wireOp",EDGE,"E224"),sQuery(id+"F4.wireOp",EDGE,"E225"),sQuery(id+"F4.wireOp",EDGE,"E226"),sQuery(id+"F4.wireOp",EDGE,"E227"),sQuery(id+"F4.wireOp",EDGE,"E228"),sQuery(id+"F4.wireOp",EDGE,"E229"),sQuery(id+"F4.wireOp",EDGE,"E230"),sQuery(id+"F4.wireOp",EDGE,"E231"),sQuery(id+"F4.wireOp",EDGE,"E232"),sQuery(id+"F4.wireOp",EDGE,"E233"),sQuery(id+"F4.wireOp",EDGE,"E234"),sQuery(id+"F4.wireOp",EDGE,"E235"),sQuery(id+"F4.wireOp",EDGE,"E236"),sQuery(id+"F4.wireOp",EDGE,"E237"),sQuery(id+"F4.wireOp",EDGE,"E238"),sQuery(id+"F4.wireOp",EDGE,"E239"),sQuery(id+"F4.wireOp",EDGE,"E240"),sQuery(id+"F4.wireOp",EDGE,"E241"),sQuery(id+"F4.wireOp",EDGE,"E242"),sQuery(id+"F4.wireOp",EDGE,"E243"),sQuery(id+"F4.wireOp",EDGE,"E244"),sQuery(id+"F4.wireOp",EDGE,"E245"),sQuery(id+"F4.wireOp",EDGE,"E246"),sQuery(id+"F4.wireOp",EDGE,"E247"),sQuery(id+"F4.wireOp",EDGE,"E248"),sQuery(id+"F4.wireOp",EDGE,"E249"),sQuery(id+"F4.wireOp",EDGE,"E250"),sQuery(id+"F4.wireOp",EDGE,"E251"),sQuery(id+"F4.wireOp",EDGE,"E252"),sQuery(id+"F4.wireOp",EDGE,"E253"),sQuery(id+"F4.wireOp",EDGE,"E254"),sQuery(id+"F4.wireOp",EDGE,"E255"),sQuery(id+"F4.wireOp",EDGE,"E256"),sQuery(id+"F4.wireOp",EDGE,"E257"),sQuery(id+"F4.wireOp",EDGE,"E258"),sQuery(id+"F4.wireOp",EDGE,"E259"),sQuery(id+"F4.wireOp",EDGE,"E260"),sQuery(id+"F4.wireOp",EDGE,"E261"),sQuery(id+"F4.wireOp",EDGE,"E262"),sQuery(id+"F4.wireOp",EDGE,"E263"),sQuery(id+"F4.wireOp",EDGE,"E264"),sQuery(id+"F4.wireOp",EDGE,"E265"),sQuery(id+"F4.wireOp",EDGE,"E266")])]});
            transform(context, id + "F6", {"entities" : qUnion([Q0]), "transformType" : TransformType.TRANSLATION_3D, "dx" : 2.97 * mm, "dy" : 11.87 * mm, "dz" : 0 * mm, "makeCopy" : false});
        }
    });
